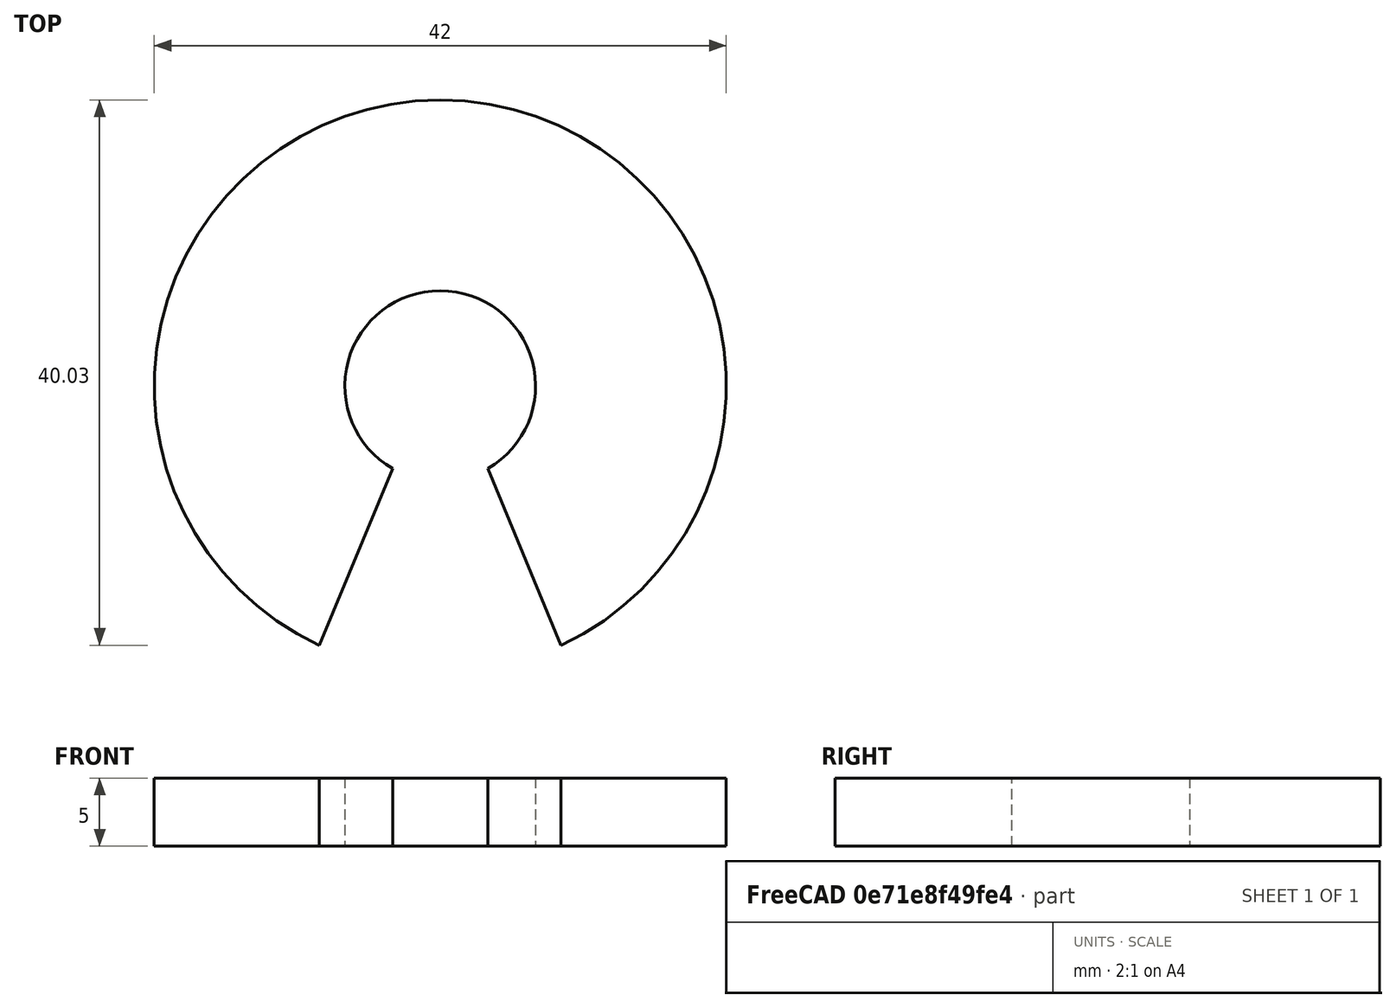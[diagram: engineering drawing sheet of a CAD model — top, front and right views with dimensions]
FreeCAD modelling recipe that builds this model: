
FCSTD DOCUMENT  (FreeCAD 0.16R6707 (Git))
Label: Logo_OSS
License: CreativeCommons Attribution-ShareAlike
LicenseURL: http://creativecommons.org/licenses/by-sa/4.0/
objects: Sketcher::SketchObject×1, PartDesign::Pad×1
note: 3 computed .brp shape members not serialized (recipe doc carries the construction recipe); baked Part::Feature solids carry a one-line shape summary decoded from their .brp

FEATURE [Sketcher::SketchObject] Sketch  label="Boceto_Open_Software"
  sketch-geometry (4):
    g0: ArcOfCircle CenterX=0 CenterY=0 CenterZ=0 NormalX=0 NormalY=0 NormalZ=1 Radius=21 StartAngle=5.14861 EndAngle=10.5594
    g1: ArcOfCircle CenterX=0 CenterY=0 CenterZ=0 NormalX=0 NormalY=0 NormalZ=1 Radius=7 StartAngle=5.23599 EndAngle=10.472
    g2: LineSegment StartX=-3.5 StartY=-6.06218 StartZ=0 EndX=-8.87288 EndY=-19.0334 EndZ=0
    g3: LineSegment StartX=3.5 StartY=-6.06218 StartZ=0 EndX=8.87288 EndY=-19.0334 EndZ=0
  constraints (12):
    c: Coincident(g1,g-1)
    c: Coincident(g0,g1)
    c: Radius(g0) = 21
    c: Radius(g1) = 7
    c: Coincident(g2,g1)
    c: Coincident(g3,g1)
    c: Coincident(g2,g0)
    c: Coincident(g3,g0)
    c: Symmetric(g0,g0,g-2)
    c: Symmetric(g1,g1,g-2)
    c: DistanceX(g1,g1) = 7
    c: Angle(g2,g3) = 0.785398
FEATURE [PartDesign::Pad] Pad  label="Logo_Open_Software"
  Length = 5
  Length2 = 100
  Sketch = -> Sketch
  Type = 0
